# Revit family: FU_Table_Sandler_Cono 4001 with Tops
name_source: partatom
category: Furniture
units: mm (PartAtom-declared; Revit-internal decimal feet)

## family parameters
Always vertical = Yes
Cut with Voids When Loaded = No
OmniClass Number = 23.40.20.00
OmniClass Title = General Furniture and Specialties
Room Calculation Point = No
Shared = No
Work Plane-Based = No

## types (5) — shared parameters
Base Finish = Metal - Lacquer - Pearl Gold
Description = Contemporary metal dining table. Max Table Top – 31.5″
Manufacturer = Sandler
Model = Cono 4001
URL = https://www.sandlerseating.com
zero-valued in all types: Default Elevation

## per-type parameters (varying)
| type | Top | Top Finish |
| Cono 4001 - 20" Top | Cono 4001 Tops : Cono Table Top - 20" - 500mm | Metal - Lacqurer - Smooth Black |
| Cono 4001 - 24" Top | Cono 4001 Tops : Cono Table Top - 24" - 600mm | Metal - Lacquer - Pearl Gold |
| Cono 4001 - 28" Top | Cono 4001 Tops : Cono Table Top - 28" - 700mm | Metal - Lacqurer - Smooth Black |
| Cono 4001 - 30" Top | Cono 4001 Tops : Cono Table Top - 30" - 750mm | Metal - Lacquer - Pearl Gold |
| Cono 4001 - 31.5" Top | Cono 4001 Tops : Cono Table Top - 31.5" - 800mm | Metal - Lacqurer - Smooth Black |

## geometry (parser evidence)
native form markers: Sweep x6
no freeform markers — native parametric forms only
